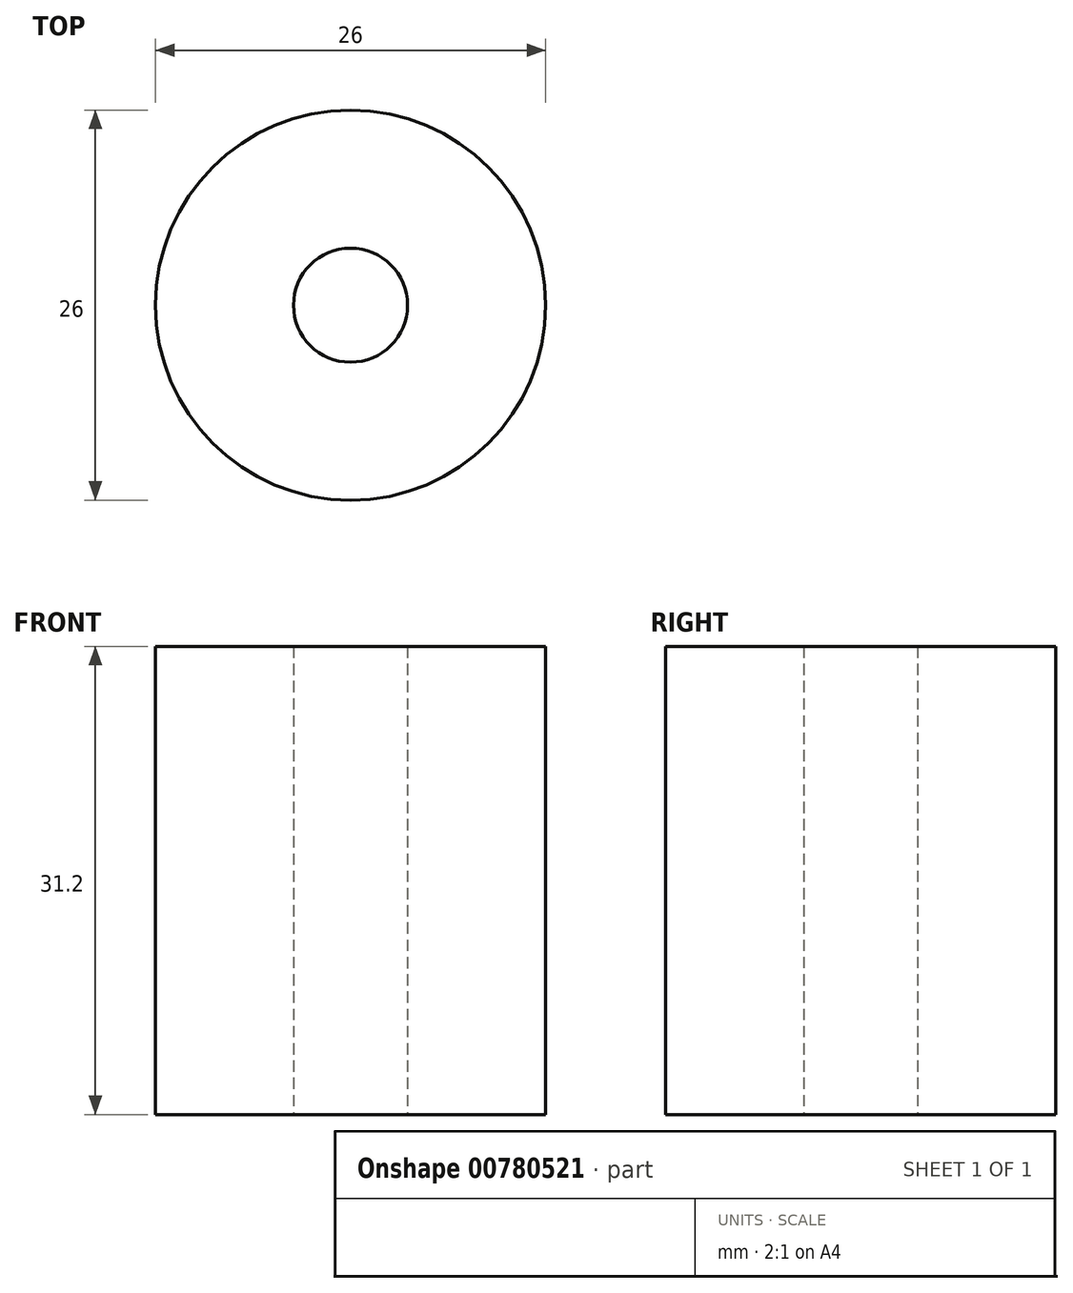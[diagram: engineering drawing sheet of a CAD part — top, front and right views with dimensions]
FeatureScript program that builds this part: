
annotation { "Feature Type Name" : "Feature", "Feature Type Description" : "" }
export const myFeature = defineFeature(function(context is Context, id is Id, definition is map)
    precondition{}
    {
        {
            var Q0;
            Q0=qCreatedBy(makeId("Top.planeOp"),FACE);
            var sketch = newSketch(context, id + "F0", { "sketchPlane" : qUnion([Q0])});
            skCircle(sketch, "E0", {"center": v(0, 0) * mm, "radius": 13 * mm});
            skCircle(sketch, "E1", {"center": v(0, 0) * mm, "radius": 3.8 * mm});
            skSolve(sketch);
        }
        {
            var Q0;
            Q0=makeQuery(id+"F0.imprint","IMPRINT",FACE,{"disambiguationData":[TD([[makeQuery(id+"F0.imprint","IMPRINT",EDGE,{"derivedFrom":sQuery(id+"F0.wireOp",EDGE,"E0")}),1.0]])]});
            extrude(context, id + "F1", {"entities" : qUnion([Q0]), "depth" : 31.2 * mm, "offsetDistance" : 25 * mm});
        }
    });
